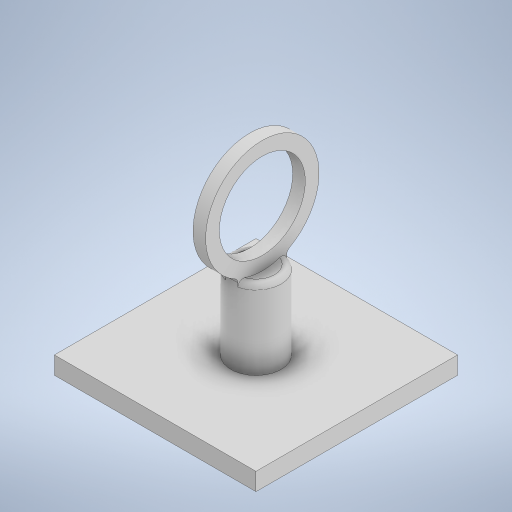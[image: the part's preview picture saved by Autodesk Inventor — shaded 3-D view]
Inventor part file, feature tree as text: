
AUTODESK INVENTOR PART (.ipt)
format: ipt  version: 2024.2 (Build 282272000, 272)  size: 297,472 bytes
history: native  units: in
note: dims shown in document units (in); Inventor stores cm internally (conversion verified against a paired STEP export)
features: sketch x3, extrude x2, plane x1, revolve x1, fillet x1
ambient origin geometry x8: Origin, YZ Plane, XZ Plane, XY Plane, X Axis, Y Axis, Z Axis, Center Point
bodies: Solid1 (feature_tree)
feature tree (8):
  extrude  "Extrusion1"  Depth=1.7717in
  plane  "Work Plane1"
  revolve  "Revolution1"  [1 undecoded]
  fillet  "Fillet1"  Radius=0.3937in
  extrude  "Extrusion2"  Depth=0.2756in
  sketch  "Sketch1"  dims[d0=1.3441in d1=1.7717in]
  sketch  "Sketch4"  dims[d2=0.1969in d3=0.0in d11=1.1811in d12=0.3937in]
  sketch  "Sketch5"  dims[d13=90.0deg d14=0.0787in d18=1.5748in d19=3.1496in d20=3.1496in d21=3.1496in d22=0.2756in d23=0.0in d9=0.0344in d10=0.0344in]
note: 1 required parameter value undecoded (feature->parameter linkage not recoverable at this tier; creation-order binding heuristic only, values carry confidence <= 0.55)
